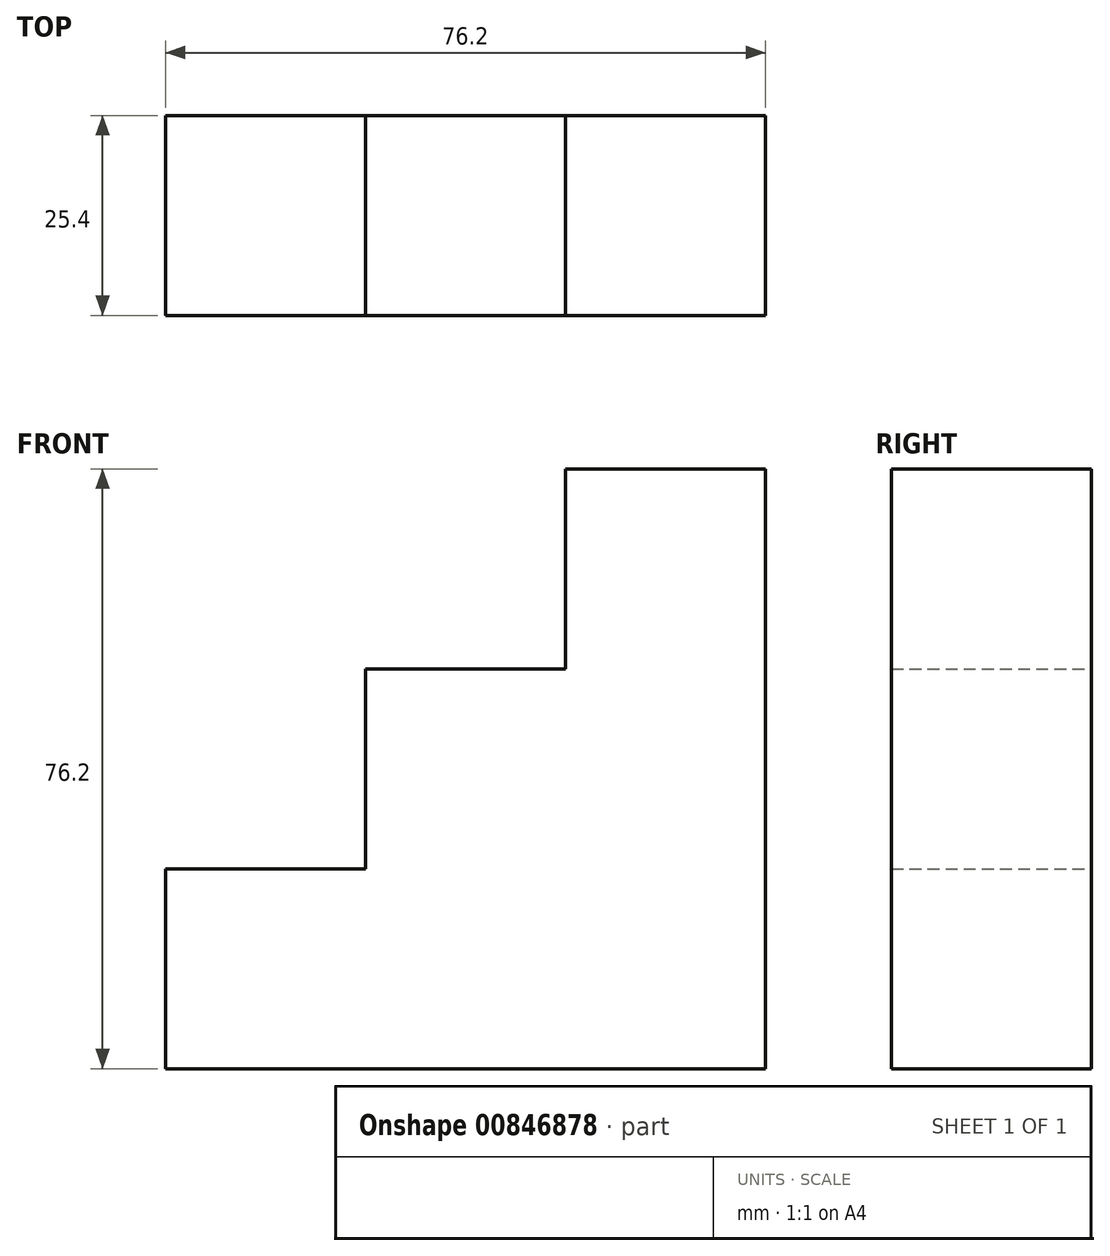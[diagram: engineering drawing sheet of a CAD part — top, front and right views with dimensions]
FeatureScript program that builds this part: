
annotation { "Feature Type Name" : "Feature", "Feature Type Description" : "" }
export const myFeature = defineFeature(function(context is Context, id is Id, definition is map)
    precondition{}
    {
        {
            var Q0;
            Q0=qCreatedBy(makeId("Front.planeOp"),FACE);
            var sketch = newSketch(context, id + "F0", { "sketchPlane" : qUnion([Q0])});
            skLineSegment(sketch, "E0", {"start": v(0, 0) * mm, "end": v(76.2, 0) * mm});
            skLineSegment(sketch, "E1", {"start": v(76.2, 0) * mm, "end": v(76.2, 76.2) * mm});
            skLineSegment(sketch, "E2", {"start": v(76.2, 76.2) * mm, "end": v(50.8, 76.2) * mm});
            skLineSegment(sketch, "E3", {"start": v(50.8, 76.2) * mm, "end": v(50.8, 50.8) * mm});
            skLineSegment(sketch, "E4", {"start": v(50.8, 50.8) * mm, "end": v(25.4, 50.8) * mm});
            skLineSegment(sketch, "E5", {"start": v(25.4, 50.8) * mm, "end": v(25.4, 25.4) * mm});
            skLineSegment(sketch, "E6", {"start": v(25.4, 25.4) * mm, "end": v(0, 25.4) * mm});
            skLineSegment(sketch, "E7", {"start": v(0, 25.4) * mm, "end": v(0, 0) * mm});
            skSolve(sketch);
        }
        {
            var Q0;
            Q0=qSketchRegion(id+"F0",true);
            extrude(context, id + "F1", {"entities" : qUnion([Q0]), "depth" : 25.4 * mm, "offsetDistance" : 25.4 * mm});
        }
    });
